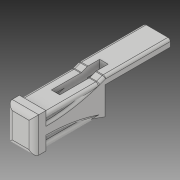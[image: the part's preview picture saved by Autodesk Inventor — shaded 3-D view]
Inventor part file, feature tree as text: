
AUTODESK INVENTOR PART (.ipt)
format: ipt  version: 2018 (Build 220112000, 112)  size: 423,936 bytes
history: native  units: mm
features: extrude x7, sketch x7, projected_geometry x3, fillet x2, chamfer x2, other x1
ambient origin geometry x8: Origin, YZ Plane, XZ Plane, XY Plane, X Axis, Y Axis, Z Axis, Center Point
bodies: Body1 (feature_tree)
feature tree (22):
  other  "ソリッド1"
  extrude  "押し出し1"  Depth=14.5mm
  extrude  "押し出し2"  Depth=11.0mm
  extrude  "押し出し4"  Depth=37.5mm TaperAngle=0.0deg
  extrude  "押し出し6"  Depth=33.0mm
  extrude  "押し出し7"  Depth=10.5mm
  fillet  "フィレット1"  Radius=37.5mm
  chamfer  "面取り2"  Distance=25.0mm
  extrude  "押し出し8"  Depth=3.5mm
  fillet  "フィレット2"  Radius=3.5mm
  extrude  "押し出し9"  Depth=5.0mm
  chamfer  "面取り3"  Distance=25.0mm
  sketch  "スケッチ1"
  sketch  "スケッチ2"
  sketch  "スケッチ4"
  projected_geometry  "投影ループ1"
  sketch  "スケッチ5"
  sketch  "スケッチ6"
  sketch  "スケッチ8"
  projected_geometry  "投影ループ2"
  sketch  "スケッチ9"
  projected_geometry  "投影ループ3"
